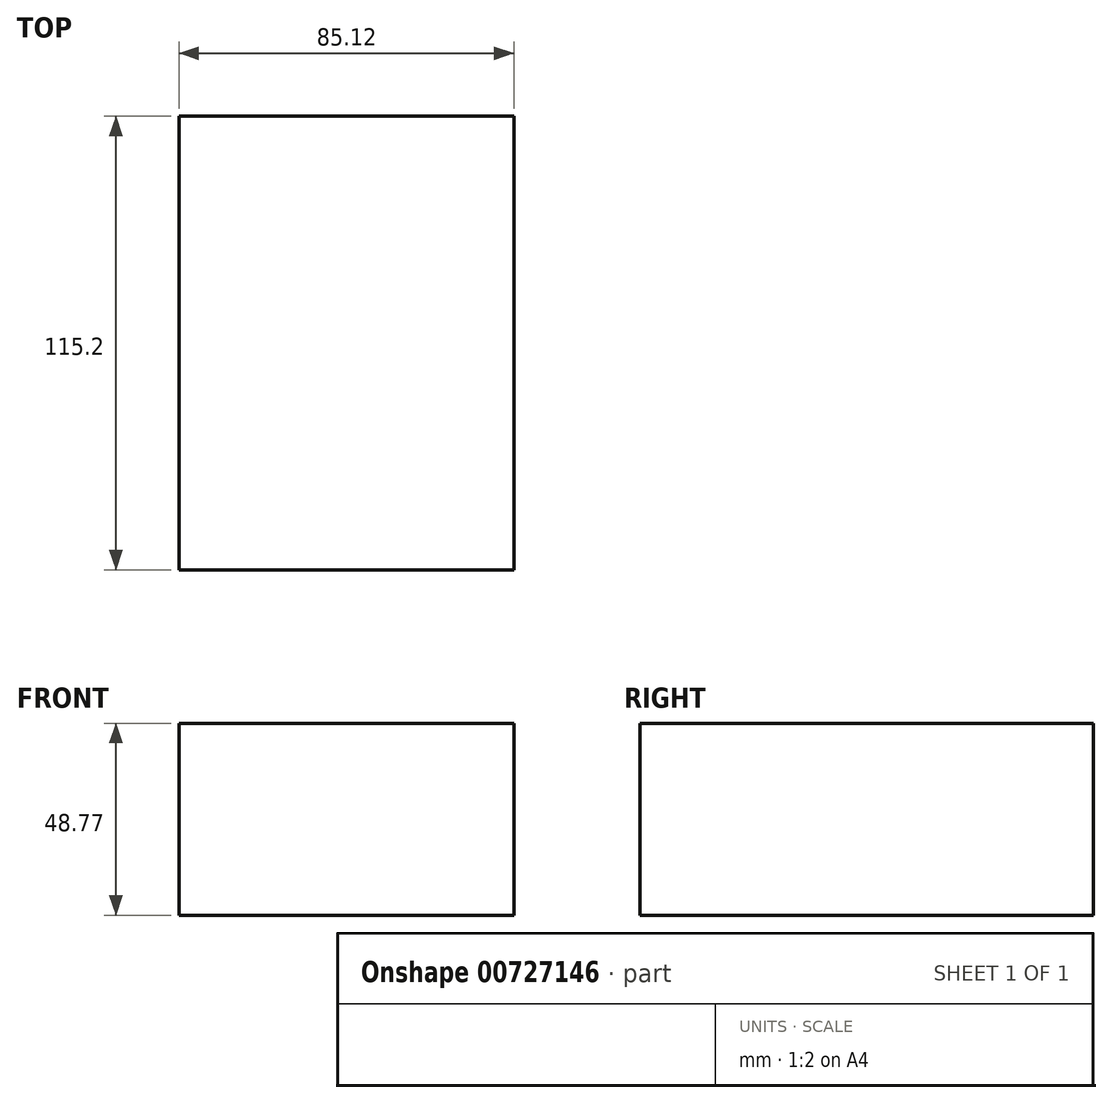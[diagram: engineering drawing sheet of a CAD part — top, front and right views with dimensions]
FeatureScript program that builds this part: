
annotation { "Feature Type Name" : "Feature", "Feature Type Description" : "" }
export const myFeature = defineFeature(function(context is Context, id is Id, definition is map)
    precondition{}
    {
        {
            var Q0;
            Q0=qCreatedBy(makeId("Top.planeOp"),FACE);
            var sketch = newSketch(context, id + "F0", { "sketchPlane" : qUnion([Q0])});
            skLineSegment(sketch, "E0.bottom", {"start": v(-42.56, 57.6) * mm, "end": v(42.56, 57.6) * mm});
            skLineSegment(sketch, "E0.top", {"start": v(-42.56, -57.6) * mm, "end": v(42.56, -57.6) * mm});
            skLineSegment(sketch, "E0.left", {"start": v(-42.56, 57.6) * mm, "end": v(-42.56, -57.6) * mm});
            skLineSegment(sketch, "E0.right", {"start": v(42.56, 57.6) * mm, "end": v(42.56, -57.6) * mm});
            skPoint(sketch, "E0.middle", {"position": v(0, 0) * mm});
            skSolve(sketch);
        }
        {
            var Q0;
            Q0=makeQuery(id+"F0.imprint","IMPRINT",FACE,{"disambiguationData":[TD([[makeQuery(id+"F0.imprint","IMPRINT",EDGE,{"derivedFrom":sQuery(id+"F0.wireOp",EDGE,"E0.bottom")}),-1.0]])]});
            extrude(context, id + "F1", {"entities" : qUnion([Q0]), "depth" : 48.77 * mm, "offsetDistance" : 25.4 * mm});
        }
        {
            var Q0;
            Q0=makeQuery(id+"F1.opExtrude","SWEPT_FACE",FACE,{"disambiguationData":[OSD([sQuery(id+"F0.wireOp",EDGE,"E0.right")])]});
            var sketch = newSketch(context, id + "F2", { "sketchPlane" : qUnion([Q0])});
            skSolve(sketch);
        }
        {
            var Q0;
            {var subQ0=sQuery(id+"F0.wireOp",EDGE,"E0.right");Q0=makeQuery(id+"F2.imprint","IMPRINT",FACE,{"disambiguationData":[TD([[makeQuery(id+"F2.imprint","IMPRINT",EDGE,{"derivedFrom":makeQuery(id+"F1.opExtrude","CAP_EDGE",EDGE,{"disambiguationData":[OSD([subQ0])],"isStart":true})}),-1.0]])]});}
            extrude(context, id + "F3", {"entities" : qUnion([Q0]), "operationType" : NewBodyOperationType.ADD, "oppositeDirection" : true, "depth" : 67.82 * mm, "offsetDistance" : 25.4 * mm});
        }
    });
